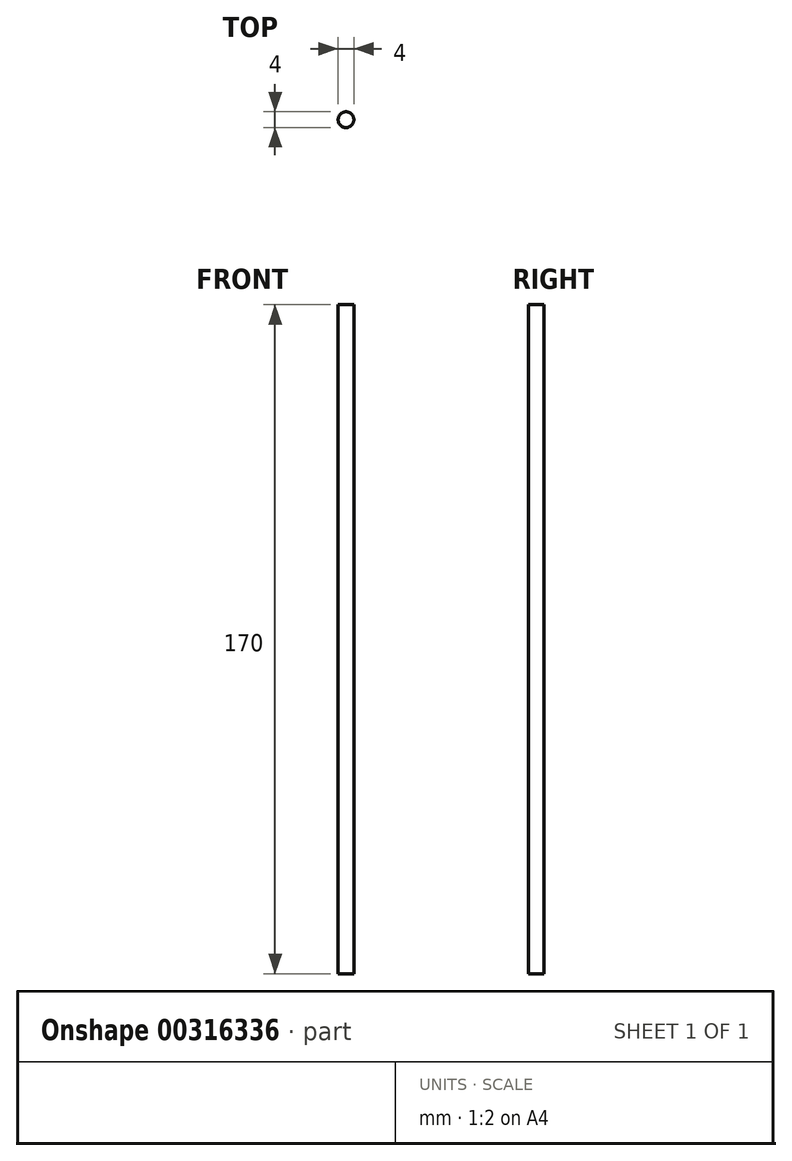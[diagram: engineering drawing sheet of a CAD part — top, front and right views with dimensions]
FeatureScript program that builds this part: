
annotation { "Feature Type Name" : "Feature", "Feature Type Description" : "" }
export const myFeature = defineFeature(function(context is Context, id is Id, definition is map)
    precondition{}
    {
        {
            var Q0;
            Q0=qCreatedBy(makeId("Top.planeOp"),FACE);
            var sketch = newSketch(context, id + "F0", { "sketchPlane" : qUnion([Q0])});
            skCircle(sketch, "E0", {"center": v(0, 0) * mm, "radius": 2 * mm});
            skSolve(sketch);
        }
        {
            var Q0;
            Q0 = qSketchRegion(id + "F0", true);
            extrude(context, id + "F1", {"entities" : qUnion([Q0]), "depth" : 170 * mm});
        }
    });
